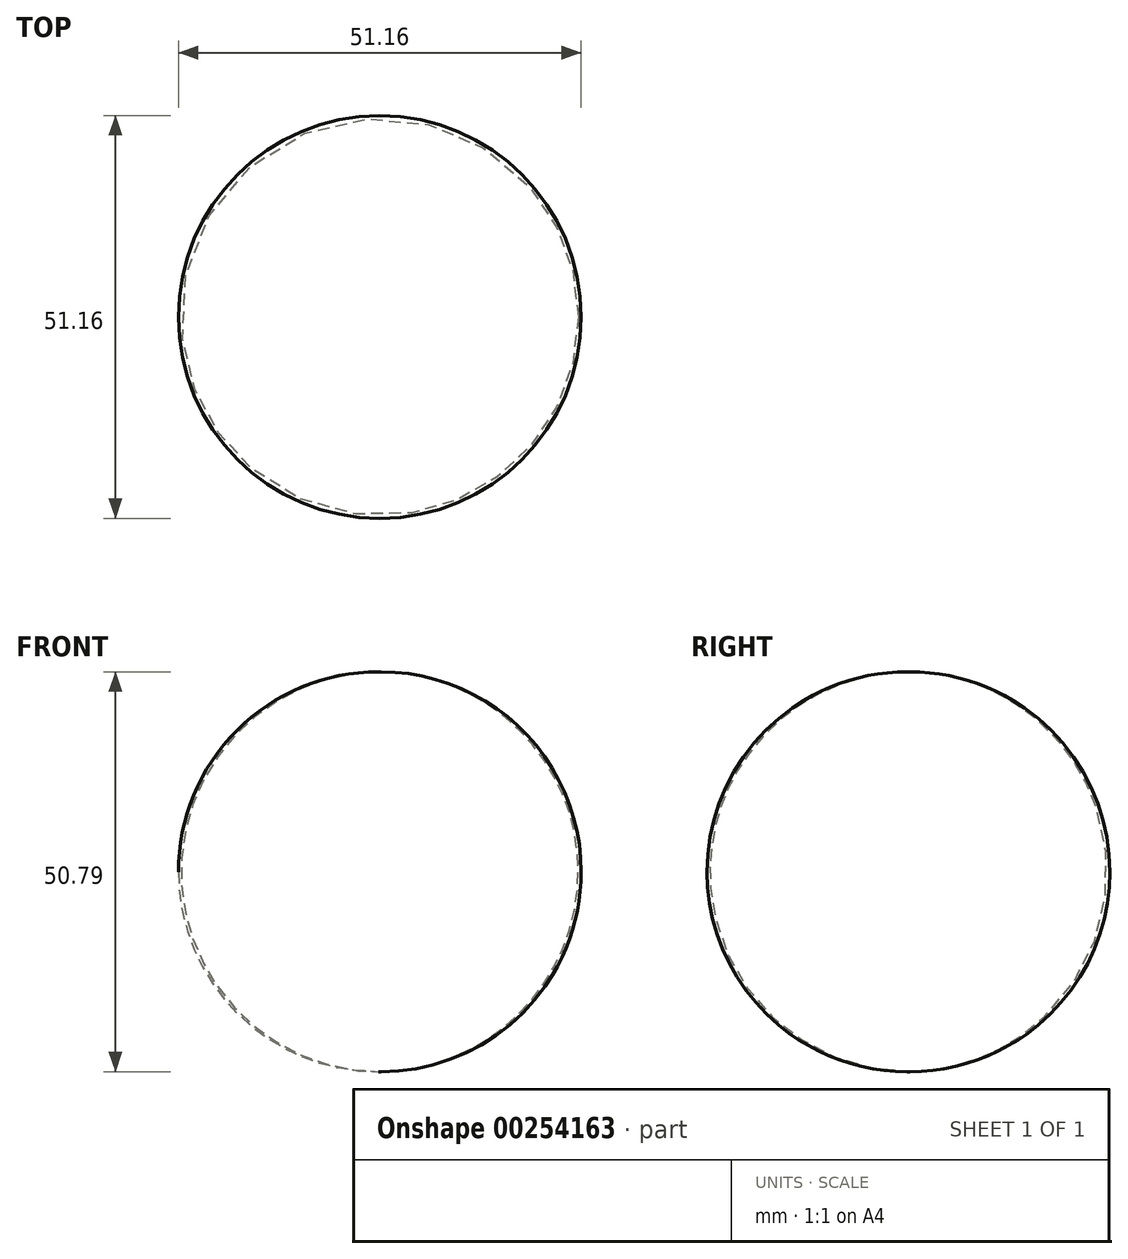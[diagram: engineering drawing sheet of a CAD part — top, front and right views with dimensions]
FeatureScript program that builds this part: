
annotation { "Feature Type Name" : "Feature", "Feature Type Description" : "" }
export const myFeature = defineFeature(function(context is Context, id is Id, definition is map)
    precondition{}
    {
        {
            var Q0;
            Q0=qCreatedBy(makeId("Front.planeOp"),FACE);
            var sketch = newSketch(context, id + "F0", { "sketchPlane" : qUnion([Q0])});
            skLineSegment(sketch, "E0", {"start": v(0, 0) * mm, "end": v(0, 50.8) * mm});
            skArc(sketch, "E1", {"start": v(0, 0) * mm, "mid": v(25.58, 25.4) * mm, "end": v(0, 50.8) * mm});
            skSolve(sketch);
        }
        {
            var Q0;
            Q0=makeQuery(id+"F0.imprint","IMPRINT",FACE,{"disambiguationData":[TD([[makeQuery(id+"F0.imprint","IMPRINT",EDGE,{"derivedFrom":sQuery(id+"F0.wireOp",EDGE,"E0")}),-1.0]])]});
            var Q1;
            Q1=sQuery(id+"F0.wireOp",EDGE,"E0");
            revolve(context, id + "F1", {"entities" : qUnion([Q0]), "axis" : qUnion([Q1]), "revolveType" : RevolveType.FULL});
        }
    });
